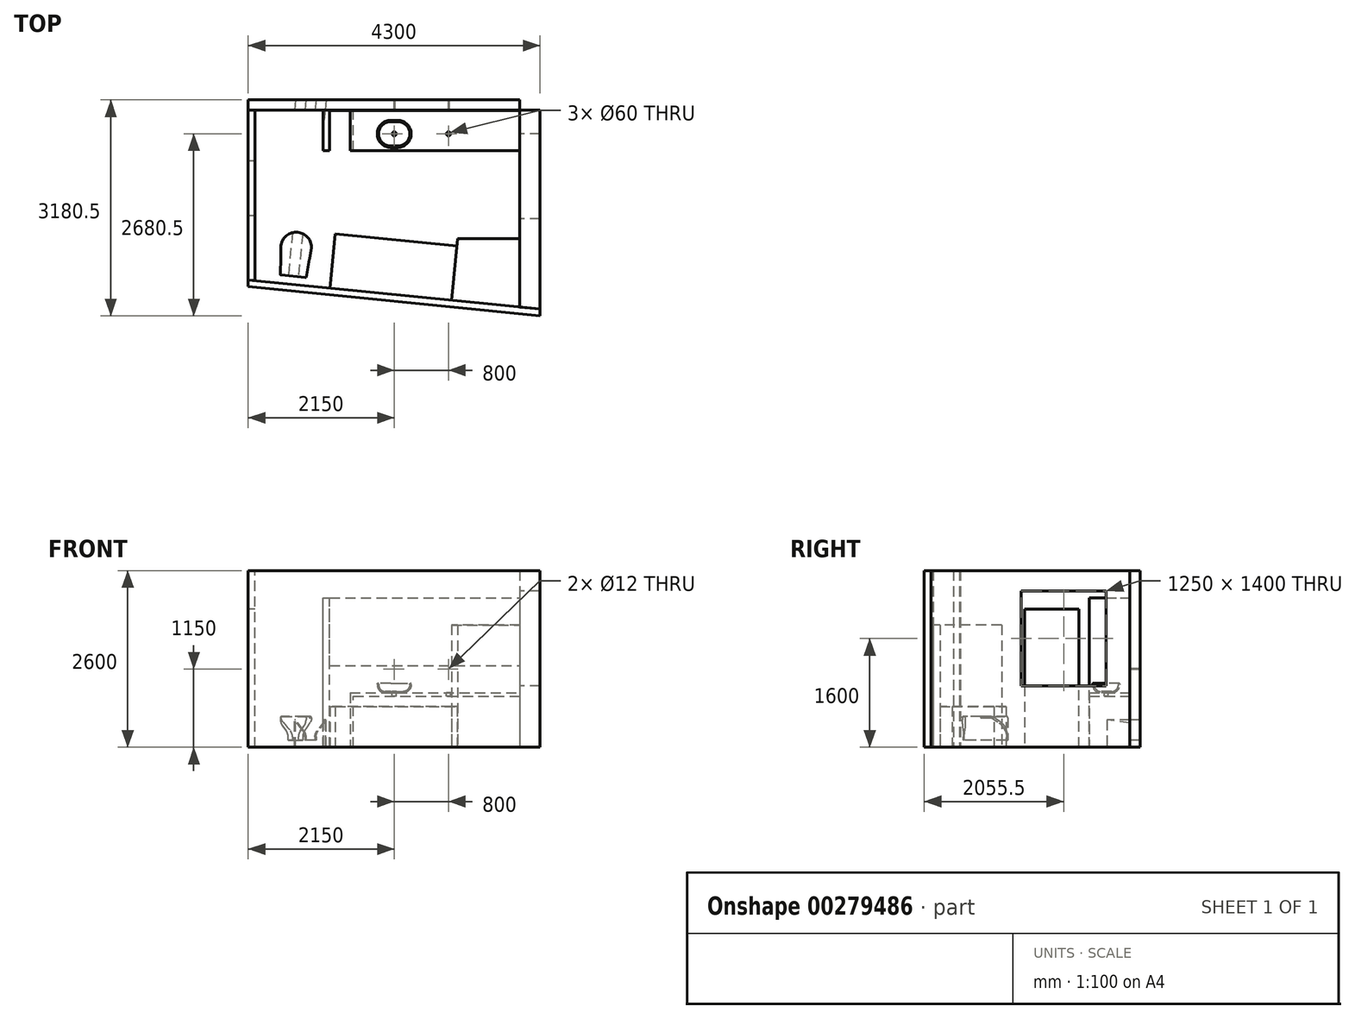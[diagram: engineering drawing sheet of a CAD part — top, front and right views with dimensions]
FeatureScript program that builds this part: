
annotation { "Feature Type Name" : "Feature", "Feature Type Description" : "" }
export const myFeature = defineFeature(function(context is Context, id is Id, definition is map)
    precondition{}
    {
        {
            var Q0;
            Q0=qCreatedBy(makeId("Front.planeOp"),FACE);
            var sketch = newSketch(context, id + "F0", { "sketchPlane" : qUnion([Q0])});
            skLineSegment(sketch, "E0.bottom", {"start": v(-1250, 800) * mm, "end": v(1250, 800) * mm});
            skLineSegment(sketch, "E0.top", {"start": v(-1250, 0) * mm, "end": v(1250, 0) * mm});
            skLineSegment(sketch, "E0.left", {"start": v(-1250, 800) * mm, "end": v(-1250, 0) * mm});
            skLineSegment(sketch, "E0.right", {"start": v(1250, 800) * mm, "end": v(1250, 0) * mm});
            skPoint(sketch, "E1", {"position": v(0, 800) * mm});
            skPoint(sketch, "E2", {"position": v(-1250, 400) * mm});
            skLineSegment(sketch, "E3", {"start": v(-1200, 0) * mm, "end": v(-1200, 750) * mm});
            skLineSegment(sketch, "E4", {"start": v(-1200, 750) * mm, "end": v(1250, 750) * mm});
            skSolve(sketch);
        }
        {
            var Q0;
            {var subQ1=sQuery(id+"F0.wireOp",EDGE,"E0.bottom");Q0=makeQuery(id+"F0.imprint","IMPRINT",FACE,{"disambiguationData":[TD([[makeQuery(id+"F0.imprint","IMPRINT",EDGE,{"derivedFrom":subQ1}),-1.0]])]});}
            extrude(context, id + "F1", {"entities" : qUnion([Q0]), "depth" : 600 * mm});
        }
        {
            var Q0;
            Q0=makeQuery(id+"F1.opExtrude","SWEPT_FACE",FACE,{"disambiguationData":[OSD([sQuery(id+"F0.wireOp",EDGE,"E0.bottom")])]});
            var sketch = newSketch(context, id + "F2", { "sketchPlane" : qUnion([Q0])});
            skLineSegment(sketch, "E5.0", {"start": v(-1250, 0) * mm, "end": v(1250, 0) * mm});
            skLineSegment(sketch, "E6.0", {"start": v(-1250, -600) * mm, "end": v(-1250, 0) * mm});
            skLineSegment(sketch, "E7.0", {"start": v(-1250, -600) * mm, "end": v(1250, -600) * mm});
            skLineSegment(sketch, "E8.0", {"start": v(1250, -600) * mm, "end": v(1250, 0) * mm});
            skLineSegment(sketch, "E9", {"start": v(-600, 54.18) * mm, "end": v(-600, -682.46) * mm, "construction": true});
            skLineSegment(sketch, "E10", {"start": v(200, 52.3) * mm, "end": v(200, -699.42) * mm, "construction": true});
            skLineSegment(sketch, "E11.bottom", {"start": v(-850, -150) * mm, "end": v(-350, -150) * mm});
            skLineSegment(sketch, "E11.top", {"start": v(-850, -550) * mm, "end": v(-350, -550) * mm});
            skLineSegment(sketch, "E11.left", {"start": v(-850, -150) * mm, "end": v(-850, -550) * mm});
            skLineSegment(sketch, "E11.right", {"start": v(-350, -150) * mm, "end": v(-350, -550) * mm});
            skLineSegment(sketch, "E12", {"start": v(-850, -350) * mm, "end": v(200, -350) * mm, "construction": true});
            skSolve(sketch);
        }
        {
            var Q0;
            Q0=makeQuery(id+"F2.imprint","IMPRINT",FACE,{"disambiguationData":[TD([[makeQuery(id+"F2.imprint","IMPRINT",EDGE,{"derivedFrom":sQuery(id+"F2.wireOp",EDGE,"E11.bottom")}),-1.0]])]});
            extrude(context, id + "F3", {"entities" : qUnion([Q0]), "depth" : 140 * mm});
        }
        {
            var Q0;
            Q0=makeQuery(id+"F3.opExtrude","SWEPT_EDGE",EDGE,{"disambiguationData":[OSD([sQuery(id+"F2.wireOp",EDGE,"E11.top"),sQuery(id+"F2.wireOp",EDGE,"E11.left")])]});
            var Q1;
            Q1=makeQuery(id+"F3.opExtrude","SWEPT_EDGE",EDGE,{"disambiguationData":[OSD([sQuery(id+"F2.wireOp",EDGE,"E11.top"),sQuery(id+"F2.wireOp",EDGE,"E11.right")])]});
            var Q2;
            Q2=makeQuery(id+"F3.opExtrude","SWEPT_EDGE",EDGE,{"disambiguationData":[OSD([sQuery(id+"F2.wireOp",EDGE,"E11.bottom"),sQuery(id+"F2.wireOp",EDGE,"E11.right")])]});
            var Q3;
            Q3=makeQuery(id+"F3.opExtrude","SWEPT_EDGE",EDGE,{"disambiguationData":[OSD([sQuery(id+"F2.wireOp",EDGE,"E11.bottom"),sQuery(id+"F2.wireOp",EDGE,"E11.left")])]});
            fillet(context, id + "F4", {"entities" : qUnion([Q0, Q1, Q2, Q3]), "radius" : 200 * mm, "tangentPropagation" : true, "allowEdgeOverflow" : false});
        }
        {
            var Q0;
            {var subQ0=sQuery(id+"F2.wireOp",EDGE,"E11.right");var subQ1=sQuery(id+"F2.wireOp",EDGE,"E11.bottom");Q0=makeQuery(id+"F4.opFillet","BLEND_EDGE",EDGE,{"blendedFrom":[makeQuery(id+"F3.opExtrude","SWEPT_EDGE",EDGE,{"disambiguationData":[OSD([subQ1,subQ0])]}),makeQuery(id+"F3.opExtrude","CAP_FACE",FACE,{"disambiguationData":[OSD([subQ1,sQuery(id+"F2.wireOp",EDGE,"E11.top"),sQuery(id+"F2.wireOp",EDGE,"E11.left"),subQ0])],"isStart":true})],"blendedInto":[makeQuery(id+"F3.opExtrude","CAP_FACE",FACE,{"disambiguationData":[OSD([subQ1,sQuery(id+"F2.wireOp",EDGE,"E11.top"),sQuery(id+"F2.wireOp",EDGE,"E11.left"),subQ0])],"isStart":true})]});}
            var Q1;
            Q1=makeQuery(id+"F3.opExtrude","CAP_EDGE",EDGE,{"disambiguationData":[OSD([sQuery(id+"F2.wireOp",EDGE,"E11.top")])],"isStart":true});
            var Q2;
            {var subQ0=sQuery(id+"F2.wireOp",EDGE,"E11.left");var subQ1=sQuery(id+"F2.wireOp",EDGE,"E11.bottom");Q2=makeQuery(id+"F4.opFillet","BLEND_EDGE",EDGE,{"blendedFrom":[makeQuery(id+"F3.opExtrude","SWEPT_EDGE",EDGE,{"disambiguationData":[OSD([subQ1,subQ0])]}),makeQuery(id+"F3.opExtrude","CAP_FACE",FACE,{"disambiguationData":[OSD([subQ1,sQuery(id+"F2.wireOp",EDGE,"E11.top"),subQ0,sQuery(id+"F2.wireOp",EDGE,"E11.right")])],"isStart":true})],"blendedInto":[makeQuery(id+"F3.opExtrude","CAP_FACE",FACE,{"disambiguationData":[OSD([subQ1,sQuery(id+"F2.wireOp",EDGE,"E11.top"),subQ0,sQuery(id+"F2.wireOp",EDGE,"E11.right")])],"isStart":true})]});}
            var Q3;
            Q3=makeQuery(id+"F3.opExtrude","CAP_EDGE",EDGE,{"disambiguationData":[OSD([sQuery(id+"F2.wireOp",EDGE,"E11.bottom")])],"isStart":true});
            fillet(context, id + "F5", {"entities" : qUnion([Q0, Q1, Q2, Q3]), "radius" : 120 * mm, "tangentPropagation" : true, "allowEdgeOverflow" : false});
        }
        {
            var Q0;
            Q0=makeQuery(id+"F3.opExtrude","CAP_FACE",FACE,{"disambiguationData":[OSD([sQuery(id+"F2.wireOp",EDGE,"E11.bottom"),sQuery(id+"F2.wireOp",EDGE,"E11.top"),sQuery(id+"F2.wireOp",EDGE,"E11.left"),sQuery(id+"F2.wireOp",EDGE,"E11.right")])],"isStart":false});
            shell(context, id + "F6", {"entities" : qUnion([Q0]), "thickness" : 20 * mm});
        }
        {
            var Q0;
            {var subQ0=sQuery(id+"F2.wireOp",EDGE,"E11.right");var subQ1=sQuery(id+"F2.wireOp",EDGE,"E11.bottom");Q0=makeQuery(id+"F4.opFillet","BLEND_EDGE",EDGE,{"blendedFrom":[makeQuery(id+"F3.opExtrude","SWEPT_EDGE",EDGE,{"disambiguationData":[OSD([subQ1,subQ0])]}),makeQuery(id+"F3.opExtrude","CAP_FACE",FACE,{"disambiguationData":[OSD([subQ1,sQuery(id+"F2.wireOp",EDGE,"E11.top"),sQuery(id+"F2.wireOp",EDGE,"E11.left"),subQ0])],"isStart":false})],"blendedInto":[makeQuery(id+"F3.opExtrude","CAP_FACE",FACE,{"disambiguationData":[OSD([subQ1,sQuery(id+"F2.wireOp",EDGE,"E11.top"),sQuery(id+"F2.wireOp",EDGE,"E11.left"),subQ0])],"isStart":false})]});}
            var Q1;
            Q1=makeQuery(id+"F3.opExtrude","CAP_EDGE",EDGE,{"disambiguationData":[OSD([sQuery(id+"F2.wireOp",EDGE,"E11.bottom")])],"isStart":false});
            var Q2;
            {var subQ0=sQuery(id+"F2.wireOp",EDGE,"E11.left");var subQ1=sQuery(id+"F2.wireOp",EDGE,"E11.bottom");Q2=makeQuery(id+"F4.opFillet","BLEND_EDGE",EDGE,{"blendedFrom":[makeQuery(id+"F3.opExtrude","SWEPT_EDGE",EDGE,{"disambiguationData":[OSD([subQ1,subQ0])]}),makeQuery(id+"F3.opExtrude","CAP_FACE",FACE,{"disambiguationData":[OSD([subQ1,sQuery(id+"F2.wireOp",EDGE,"E11.top"),subQ0,sQuery(id+"F2.wireOp",EDGE,"E11.right")])],"isStart":false})],"blendedInto":[makeQuery(id+"F3.opExtrude","CAP_FACE",FACE,{"disambiguationData":[OSD([subQ1,sQuery(id+"F2.wireOp",EDGE,"E11.top"),subQ0,sQuery(id+"F2.wireOp",EDGE,"E11.right")])],"isStart":false})]});}
            var Q3;
            Q3=makeQuery(id+"F3.opExtrude","CAP_EDGE",EDGE,{"disambiguationData":[OSD([sQuery(id+"F2.wireOp",EDGE,"E11.top")])],"isStart":false});
            fillet(context, id + "F7", {"entities" : qUnion([Q0, Q1, Q2, Q3]), "radius" : 10 * mm, "tangentPropagation" : true, "allowEdgeOverflow" : false});
        }
        {
            var Q0;
            {var subQ0=sQuery(id+"F2.wireOp",EDGE,"E11.top");Q0=makeQuery(id+"F6.opShell","OFFSET_EDGE",EDGE,{"disambiguationData":[OSD([subQ0]),TDD([makeQuery(id+"F3.opExtrude","CAP_EDGE",EDGE,{"disambiguationData":[OSD([subQ0])],"isStart":false})])]});}
            var Q1;
            {var subQ0=sQuery(id+"F2.wireOp",EDGE,"E11.right");var subQ1=sQuery(id+"F2.wireOp",EDGE,"E11.left");var subQ2=sQuery(id+"F2.wireOp",EDGE,"E11.top");var subQ3=sQuery(id+"F2.wireOp",EDGE,"E11.bottom");Q1=makeQuery(id+"F6.opShell","OFFSET_EDGE",EDGE,{"disambiguationData":[OSD([subQ3,subQ2,subQ1,subQ0]),TDD([makeQuery(id+"F4.opFillet","BLEND_EDGE",EDGE,{"blendedFrom":[makeQuery(id+"F3.opExtrude","SWEPT_EDGE",EDGE,{"disambiguationData":[OSD([subQ3,subQ1])]}),makeQuery(id+"F3.opExtrude","CAP_FACE",FACE,{"disambiguationData":[OSD([subQ3,subQ2,subQ1,subQ0])],"isStart":false})],"blendedInto":[makeQuery(id+"F3.opExtrude","CAP_FACE",FACE,{"disambiguationData":[OSD([subQ3,subQ2,subQ1,subQ0])],"isStart":false})]})])]});}
            var Q2;
            {var subQ0=sQuery(id+"F2.wireOp",EDGE,"E11.right");var subQ1=sQuery(id+"F2.wireOp",EDGE,"E11.left");var subQ2=sQuery(id+"F2.wireOp",EDGE,"E11.top");var subQ3=sQuery(id+"F2.wireOp",EDGE,"E11.bottom");Q2=makeQuery(id+"F6.opShell","OFFSET_EDGE",EDGE,{"disambiguationData":[OSD([subQ3,subQ2,subQ1,subQ0]),TDD([makeQuery(id+"F4.opFillet","BLEND_EDGE",EDGE,{"blendedFrom":[makeQuery(id+"F3.opExtrude","SWEPT_EDGE",EDGE,{"disambiguationData":[OSD([subQ3,subQ0])]}),makeQuery(id+"F3.opExtrude","CAP_FACE",FACE,{"disambiguationData":[OSD([subQ3,subQ2,subQ1,subQ0])],"isStart":false})],"blendedInto":[makeQuery(id+"F3.opExtrude","CAP_FACE",FACE,{"disambiguationData":[OSD([subQ3,subQ2,subQ1,subQ0])],"isStart":false})]})])]});}
            var Q3;
            {var subQ0=sQuery(id+"F2.wireOp",EDGE,"E11.bottom");Q3=makeQuery(id+"F6.opShell","OFFSET_EDGE",EDGE,{"disambiguationData":[OSD([subQ0]),TDD([makeQuery(id+"F3.opExtrude","CAP_EDGE",EDGE,{"disambiguationData":[OSD([subQ0])],"isStart":false})])]});}
            fillet(context, id + "F8", {"entities" : qUnion([Q0, Q1, Q2, Q3]), "radius" : 10 * mm, "tangentPropagation" : true, "allowEdgeOverflow" : false});
        }
        {
            var Q0;
            {var subQ0=sQuery(id+"F2.wireOp",EDGE,"E11.right");var subQ1=sQuery(id+"F2.wireOp",EDGE,"E11.left");var subQ2=sQuery(id+"F2.wireOp",EDGE,"E11.top");var subQ3=sQuery(id+"F2.wireOp",EDGE,"E11.bottom");Q0=makeQuery(id+"F6.opShell","OFFSET_FACE",FACE,{"disambiguationData":[OSD([subQ3,subQ2,subQ1,subQ0]),TDD([makeQuery(id+"F3.opExtrude","CAP_FACE",FACE,{"disambiguationData":[OSD([subQ3,subQ2,subQ1,subQ0])],"isStart":true})])]});}
            var sketch = newSketch(context, id + "F9", { "sketchPlane" : qUnion([Q0])});
            skLineSegment(sketch, "E13.0", {"start": v(-650, -270) * mm, "end": v(-550, -270) * mm});
            skLineSegment(sketch, "E14.0", {"start": v(-550, -430) * mm, "end": v(-650, -430) * mm});
            skLineSegment(sketch, "E15", {"start": v(-600, -430) * mm, "end": v(-600, -270) * mm, "construction": true});
            skPoint(sketch, "E16", {"position": v(-600, -350) * mm});
            skCircle(sketch, "E17", {"center": v(-600, -350) * mm, "radius": 30 * mm});
            skSolve(sketch);
        }
        {
            var Q0;
            Q0=makeQuery(id+"F9.imprint","IMPRINT",FACE,{"disambiguationData":[TD([[makeQuery(id+"F9.imprint","IMPRINT",EDGE,{"derivedFrom":sQuery(id+"F9.wireOp",EDGE,"E17")}),1.0]])]});
            extrude(context, id + "F10", {"entities" : qUnion([Q0]), "operationType" : NewBodyOperationType.REMOVE, "endBound" : BoundingType.THROUGH_ALL, "oppositeDirection" : true, "depth" : 25 * mm});
        }
        {
            var Q0;
            Q0=sQuery(id+"F2.wireOp",VERTEX,"E12.end");
            var Q1;
            Q1=makeQuery(id+"F1.opExtrude","SWEPT_BODY",BODY,{"disambiguationData":[OSD([sQuery(id+"F0.wireOp",EDGE,"E0.bottom"),sQuery(id+"F0.wireOp",EDGE,"E0.top"),sQuery(id+"F0.wireOp",EDGE,"E0.left"),sQuery(id+"F0.wireOp",EDGE,"E0.right"),sQuery(id+"F0.wireOp",EDGE,"E3"),sQuery(id+"F0.wireOp",EDGE,"E4")])]});
            hole(context, id + "F11", {"style" : HoleStyle.SIMPLE, "endStyle" : HoleEndStyle.BLIND, "holeDiameter" : 60 * mm, "holeDepth" : 170 * mm, "tappedDepth" : 12 * mm, "tapClearance" : 3, "locations" : qUnion([Q0]), "scope" : qUnion([Q1])});
        }
        {
            var Q0;
            Q0=makeQuery(id+"F1.opExtrude","CAP_FACE",FACE,{"disambiguationData":[OSD([sQuery(id+"F0.wireOp",EDGE,"E0.bottom"),sQuery(id+"F0.wireOp",EDGE,"E0.top"),sQuery(id+"F0.wireOp",EDGE,"E0.left"),sQuery(id+"F0.wireOp",EDGE,"E0.right"),sQuery(id+"F0.wireOp",EDGE,"E3"),sQuery(id+"F0.wireOp",EDGE,"E4")])],"isStart":true});
            var sketch = newSketch(context, id + "F12", { "sketchPlane" : qUnion([Q0])});
            skLineSegment(sketch, "E18.0", {"start": v(2750, 0) * mm, "end": v(-1250, 0) * mm});
            skLineSegment(sketch, "E19.0", {"start": v(-1250, 2600) * mm, "end": v(-1250, 0) * mm});
            skPoint(sketch, "E20.orphan", {"position": v(1200, 0) * mm});
            skPoint(sketch, "E21.orphan", {"position": v(-1250, 750) * mm});
            skLineSegment(sketch, "E22", {"start": v(-1250, 2600) * mm, "end": v(2750, 2600) * mm});
            skLineSegment(sketch, "E23", {"start": v(2750, 2600) * mm, "end": v(2750, 0) * mm});
            skPoint(sketch, "E24.orphan", {"position": v(1250, 0) * mm});
            skPoint(sketch, "E25.orphan", {"position": v(-1250, 800) * mm});
            skSolve(sketch);
        }
        {
            var Q0;
            {var subQ1=sQuery(id+"F12.wireOp",EDGE,"E22");Q0=makeQuery(id+"F12.imprint","IMPRINT",FACE,{"disambiguationData":[TD([[makeQuery(id+"F12.imprint","IMPRINT",EDGE,{"derivedFrom":subQ1}),-1.0]])]});}
            var Q1;
            {var subQ1=makeQuery(id+"F1.opExtrude","CAP_EDGE",EDGE,{"disambiguationData":[OSD([sQuery(id+"F0.wireOp",EDGE,"E3")])],"isStart":true});Q1=makeQuery(id+"F12.imprint","IMPRINT",FACE,{"disambiguationData":[TD([[makeQuery(id+"F12.imprint","IMPRINT",EDGE,{"derivedFrom":subQ1}),1.0]])]});}
            var Q2;
            {var subQ1=makeQuery(id+"F1.opExtrude","CAP_EDGE",EDGE,{"disambiguationData":[OSD([sQuery(id+"F0.wireOp",EDGE,"E0.bottom")])],"isStart":true});Q2=makeQuery(id+"F12.imprint","IMPRINT",FACE,{"disambiguationData":[TD([[makeQuery(id+"F12.imprint","IMPRINT",EDGE,{"derivedFrom":subQ1}),1.0]])]});}
            extrude(context, id + "F13", {"entities" : qUnion([Q0, Q1, Q2]), "depth" : 150 * mm});
        }
        {
            var Q0;
            Q0=makeQuery(id+"F13.opExtrude","CAP_FACE",FACE,{"disambiguationData":[OSD([sQuery(id+"F12.wireOp",EDGE,"E18.0"),sQuery(id+"F12.wireOp",EDGE,"E19.0"),sQuery(id+"F12.wireOp",EDGE,"E22"),sQuery(id+"F12.wireOp",EDGE,"E23")])],"isStart":true});
            var sketch = newSketch(context, id + "F14", { "sketchPlane" : qUnion([Q0])});
            skLineSegment(sketch, "E26.0", {"start": v(-2750, 0) * mm, "end": v(1250, 0) * mm});
            skLineSegment(sketch, "E27", {"start": v(-600, 0) * mm, "end": v(-600, 1150) * mm, "construction": true});
            skLineSegment(sketch, "E28", {"start": v(200, 0) * mm, "end": v(200, 1150) * mm, "construction": true});
            skLineSegment(sketch, "E29.0", {"start": v(-630, 800) * mm, "end": v(-570, 800) * mm});
            skLineSegment(sketch, "E30.0", {"start": v(170, 800) * mm, "end": v(230, 800) * mm});
            skPoint(sketch, "E31", {"position": v(-600, 800) * mm});
            skPoint(sketch, "E32", {"position": v(200, 800) * mm});
            skPoint(sketch, "E33", {"position": v(-600, 1150) * mm});
            skPoint(sketch, "E34", {"position": v(200, 1150) * mm});
            skSolve(sketch);
        }
        {
            var Q0;
            Q0=sQuery(id+"F14.wireOp",VERTEX,"E33");
            var Q1;
            Q1=sQuery(id+"F14.wireOp",VERTEX,"E34");
            var Q2;
            Q2=makeQuery(id+"F13.opExtrude","SWEPT_BODY",BODY,{"disambiguationData":[OSD([sQuery(id+"F12.wireOp",EDGE,"E18.0"),sQuery(id+"F12.wireOp",EDGE,"E19.0"),sQuery(id+"F12.wireOp",EDGE,"E22"),sQuery(id+"F12.wireOp",EDGE,"E23")])]});
            hole(context, id + "F15", {"style" : HoleStyle.SIMPLE, "endStyle" : HoleEndStyle.BLIND, "holeDiameter" : 12 * mm, "holeDepth" : 200 * mm, "tappedDepth" : 12 * mm, "tapClearance" : 3, "locations" : qUnion([Q0, Q1]), "scope" : qUnion([Q2])});
        }
        {
            var Q0;
            Q0=makeQuery(id+"F13.opExtrude","CAP_FACE",FACE,{"disambiguationData":[OSD([sQuery(id+"F12.wireOp",EDGE,"E18.0"),sQuery(id+"F12.wireOp",EDGE,"E19.0"),sQuery(id+"F12.wireOp",EDGE,"E22"),sQuery(id+"F12.wireOp",EDGE,"E23")])],"isStart":true});
            var sketch = newSketch(context, id + "F16", { "sketchPlane" : qUnion([Q0])});
            skLineSegment(sketch, "E35.0", {"start": v(-1250, 800) * mm, "end": v(-1250, 0) * mm});
            skLineSegment(sketch, "E36.bottom", {"start": v(-1650, 0) * mm, "end": v(-1550, 0) * mm});
            skLineSegment(sketch, "E36.top", {"start": v(-1650, 2200) * mm, "end": v(-1550, 2200) * mm});
            skLineSegment(sketch, "E36.left", {"start": v(-1650, 0) * mm, "end": v(-1650, 2200) * mm});
            skLineSegment(sketch, "E36.right", {"start": v(-1550, 0) * mm, "end": v(-1550, 2200) * mm});
            skLineSegment(sketch, "E37.bottom", {"start": v(-1550, 2200) * mm, "end": v(1250, 2200) * mm});
            skLineSegment(sketch, "E37.top", {"start": v(-1550, 1200) * mm, "end": v(1250, 1200) * mm});
            skLineSegment(sketch, "E37.left", {"start": v(-1550, 2200) * mm, "end": v(-1550, 1200) * mm});
            skLineSegment(sketch, "E37.right", {"start": v(1250, 2200) * mm, "end": v(1250, 1200) * mm});
            skLineSegment(sketch, "E38.bottom", {"start": v(-2750, 0) * mm, "end": v(-2650, 0) * mm});
            skLineSegment(sketch, "E38.top", {"start": v(-2750, 2600) * mm, "end": v(-2650, 2600) * mm});
            skLineSegment(sketch, "E38.left", {"start": v(-2750, 0) * mm, "end": v(-2750, 2600) * mm});
            skLineSegment(sketch, "E38.right", {"start": v(-2650, 0) * mm, "end": v(-2650, 2600) * mm});
            skSolve(sketch);
        }
        {
            var Q0;
            Q0=makeQuery(id+"F16.imprint","IMPRINT",FACE,{"disambiguationData":[TD([[makeQuery(id+"F16.imprint","IMPRINT",EDGE,{"derivedFrom":sQuery(id+"F16.wireOp",EDGE,"E37.bottom")}),-1.0]])]});
            extrude(context, id + "F17", {"entities" : qUnion([Q0]), "depth" : 8 * mm});
        }
        {
            var Q0;
            Q0=makeQuery(id+"F16.imprint","IMPRINT",FACE,{"disambiguationData":[TD([[makeQuery(id+"F16.imprint","IMPRINT",EDGE,{"derivedFrom":sQuery(id+"F16.wireOp",EDGE,"E36.bottom")}),1.0]])]});
            extrude(context, id + "F18", {"entities" : qUnion([Q0]), "depth" : 600 * mm});
        }
        {
            var Q0;
            Q0=makeQuery(id+"F16.imprint","IMPRINT",FACE,{"disambiguationData":[TD([[makeQuery(id+"F16.imprint","IMPRINT",EDGE,{"derivedFrom":sQuery(id+"F16.wireOp",EDGE,"E38.bottom")}),1.0]])]});
            extrude(context, id + "F19", {"entities" : qUnion([Q0]), "depth" : 750 * mm});
        }
        {
            var Q0;
            Q0=makeQuery(id+"F13.opExtrude","SWEPT_FACE",FACE,{"disambiguationData":[OSD([sQuery(id+"F12.wireOp",EDGE,"E18.0")])]});
            var sketch = newSketch(context, id + "F20", { "sketchPlane" : qUnion([Q0])});
            skLineSegment(sketch, "E39.0", {"start": v(-2750, 0) * mm, "end": v(1550, 0) * mm});
            skLineSegment(sketch, "E40.0", {"start": v(-2650, 750) * mm, "end": v(-2650, 0) * mm});
            skLineSegment(sketch, "E41.0", {"start": v(-2750, 750) * mm, "end": v(-2750, 0) * mm});
            skLineSegment(sketch, "E42", {"start": v(-2750, 2500) * mm, "end": v(1550, 2930) * mm});
            skLineSegment(sketch, "E43", {"start": v(1250, 0) * mm, "end": v(1250, 2900) * mm});
            skLineSegment(sketch, "E44", {"start": v(-2650, 1550) * mm, "end": v(-2650, 2510) * mm});
            skLineSegment(sketch, "E45", {"start": v(-2750, 1550) * mm, "end": v(-2750, 2600.5) * mm});
            skLineSegment(sketch, "E46", {"start": v(-2750, 1550) * mm, "end": v(-2650, 1550) * mm});
            skLineSegment(sketch, "E47", {"start": v(-2750, 2600.5) * mm, "end": v(1550, 3030.5) * mm});
            skLineSegment(sketch, "E48", {"start": v(1550, 0) * mm, "end": v(1550, 3030.5) * mm});
            skSolve(sketch);
        }
        {
            var Q0;
            {var subQ3=sQuery(id+"F20.wireOp",EDGE,"E44");Q0=makeQuery(id+"F20.imprint","IMPRINT",FACE,{"disambiguationData":[TD([[makeQuery(id+"F20.imprint","IMPRINT",EDGE,{"derivedFrom":subQ3}),1.0]])]});}
            extrude(context, id + "F21", {"entities" : qUnion([Q0]), "oppositeDirection" : true, "depth" : 2600 * mm});
        }
        {
            var Q0;
            {var subQ6=sQuery(id+"F20.wireOp",EDGE,"E47");Q0=makeQuery(id+"F20.imprint","IMPRINT",FACE,{"disambiguationData":[TD([[makeQuery(id+"F20.imprint","IMPRINT",EDGE,{"derivedFrom":subQ6}),-1.0]])]});}
            extrude(context, id + "F22", {"entities" : qUnion([Q0]), "oppositeDirection" : true, "depth" : 2600 * mm});
        }
        {
            var Q0;
            {var subQ0=sQuery(id+"F20.wireOp",EDGE,"E43");Q0=makeQuery(id+"F20.imprint","IMPRINT",FACE,{"disambiguationData":[TD([[makeQuery(id+"F20.imprint","IMPRINT",EDGE,{"derivedFrom":subQ0}),-1.0]])]});}
            extrude(context, id + "F23", {"entities" : qUnion([Q0]), "oppositeDirection" : true, "depth" : 2600 * mm});
        }
        {
            var Q0;
            Q0=makeQuery(id+"F23.opExtrude","SWEPT_FACE",FACE,{"disambiguationData":[OSD([sQuery(id+"F20.wireOp",EDGE,"E43")])]});
            var sketch = newSketch(context, id + "F24", { "sketchPlane" : qUnion([Q0])});
            skLineSegment(sketch, "E49.0", {"start": v(0, 2600) * mm, "end": v(0, 0) * mm});
            skLineSegment(sketch, "E50.0", {"start": v(0, 0) * mm, "end": v(2900, 0) * mm});
            skLineSegment(sketch, "E51.bottom", {"start": v(350, 2300) * mm, "end": v(1600, 2300) * mm});
            skLineSegment(sketch, "E51.top", {"start": v(350, 900) * mm, "end": v(1600, 900) * mm});
            skLineSegment(sketch, "E51.left", {"start": v(350, 2300) * mm, "end": v(350, 900) * mm});
            skLineSegment(sketch, "E51.right", {"start": v(1600, 2300) * mm, "end": v(1600, 900) * mm});
            skSolve(sketch);
        }
        {
            var Q0;
            Q0=makeQuery(id+"F24.imprint","IMPRINT",FACE,{"disambiguationData":[TD([[makeQuery(id+"F24.imprint","IMPRINT",EDGE,{"derivedFrom":sQuery(id+"F24.wireOp",EDGE,"E51.bottom")}),-1.0]])]});
            extrude(context, id + "F25", {"entities" : qUnion([Q0]), "operationType" : NewBodyOperationType.REMOVE, "endBound" : BoundingType.THROUGH_ALL, "oppositeDirection" : true, "depth" : 25 * mm});
        }
        {
            var Q0;
            Q0=makeQuery(id+"F19.opExtrude","CAP_FACE",FACE,{"disambiguationData":[OSD([sQuery(id+"F16.wireOp",EDGE,"E38.bottom"),sQuery(id+"F16.wireOp",EDGE,"E38.top"),sQuery(id+"F16.wireOp",EDGE,"E38.left"),sQuery(id+"F16.wireOp",EDGE,"E38.right")])],"isStart":false});
            var sketch = newSketch(context, id + "F26", { "sketchPlane" : qUnion([Q0])});
            skLineSegment(sketch, "E52.0", {"start": v(-2650, 0) * mm, "end": v(-2650, 2600) * mm});
            skLineSegment(sketch, "E53.0", {"start": v(-2750, 2600) * mm, "end": v(-2750, 0) * mm});
            skLineSegment(sketch, "E54.0", {"start": v(-2750, 0) * mm, "end": v(-2650, 0) * mm});
            skLineSegment(sketch, "E55.0", {"start": v(-2650, 2600) * mm, "end": v(-2750, 2600) * mm});
            skLineSegment(sketch, "E56", {"start": v(-2650, 2030) * mm, "end": v(-2750, 2030) * mm});
            skSolve(sketch);
        }
        {
            var Q0;
            {var subQ0=sQuery(id+"F26.wireOp",EDGE,"E55.0");Q0=makeQuery(id+"F26.imprint","IMPRINT",FACE,{"disambiguationData":[TD([[makeQuery(id+"F26.imprint","IMPRINT",EDGE,{"derivedFrom":subQ0}),1.0]])]});}
            var Q1;
            Q1=makeQuery(id+"F21.opExtrude","SWEPT_FACE",FACE,{"disambiguationData":[OSD([sQuery(id+"F20.wireOp",EDGE,"E46")])]});
            extrude(context, id + "F27", {"entities" : qUnion([Q0]), "operationType" : NewBodyOperationType.ADD, "endBound" : BoundingType.UP_TO_SURFACE, "endBoundEntityFace" : qUnion([Q1]), "depth" : 25 * mm});
        }
        {
            var Q0;
            Q0=makeQuery(id+"F23.opExtrude","CAP_FACE",FACE,{"disambiguationData":[OSD([sQuery(id+"F20.wireOp",EDGE,"E39.0"),sQuery(id+"F20.wireOp",EDGE,"E42"),sQuery(id+"F20.wireOp",EDGE,"E43"),sQuery(id+"F20.wireOp",EDGE,"E48")])],"isStart":true});
            var sketch = newSketch(context, id + "F28", { "sketchPlane" : qUnion([Q0])});
            skLineSegment(sketch, "E57.0", {"start": v(1250, 0) * mm, "end": v(1250, 2900) * mm});
            skLineSegment(sketch, "E58.0", {"start": v(245.01, 2799.5) * mm, "end": v(1250, 2900) * mm});
            skLineSegment(sketch, "E59", {"start": v(1250, 1890) * mm, "end": v(335.96, 1890) * mm});
            skLineSegment(sketch, "E60", {"start": v(335.96, 1890) * mm, "end": v(245.01, 2799.5) * mm});
            skPoint(sketch, "E61.orphan", {"position": v(-2750, 2500) * mm});
            skPoint(sketch, "E62.orphan", {"position": v(1550, 2930) * mm});
            skLineSegment(sketch, "E63", {"start": v(245.01, 2799.5) * mm, "end": v(-1546.05, 2620.4) * mm});
            skLineSegment(sketch, "E64", {"start": v(-1546.05, 2620.4) * mm, "end": v(-1466.45, 1824.36) * mm});
            skLineSegment(sketch, "E65", {"start": v(-1466.45, 1824.36) * mm, "end": v(324.62, 2003.47) * mm});
            skLineSegment(sketch, "E66", {"start": v(-1546.05, 2620.4) * mm, "end": v(-2650, 2510) * mm});
            skLineSegment(sketch, "E67.0", {"start": v(-2650, 1550) * mm, "end": v(-2650, 2510) * mm});
            skPoint(sketch, "E68", {"position": v(-2098.03, 2565.2) * mm});
            skLineSegment(sketch, "E69", {"start": v(-2098.03, 2565.2) * mm, "end": v(-2021.4, 1799.02) * mm, "construction": true});
            skLineSegment(sketch, "E70", {"start": v(-1534.11, 2501) * mm, "end": v(-2650, 2389.4) * mm});
            skCircle(sketch, "E71", {"center": v(-2043.8, 2022.9) * mm, "radius": 225 * mm});
            skLineSegment(sketch, "E72", {"start": v(-1822.58, 2064) * mm, "end": v(-1897.03, 2464.7) * mm});
            skLineSegment(sketch, "E73", {"start": v(-2268.77, 2019.38) * mm, "end": v(-2275.14, 2426.89) * mm});
            skLineSegment(sketch, "E74", {"start": v(-1897.03, 2464.7) * mm, "end": v(-2275.14, 2426.89) * mm, "construction": true});
            skPoint(sketch, "E75", {"position": v(-2086.09, 2445.8) * mm});
            skSolve(sketch);
        }
        {
            var Q0;
            {var subQ3=sQuery(id+"F28.wireOp",EDGE,"E63");Q0=makeQuery(id+"F28.imprint","IMPRINT",FACE,{"disambiguationData":[TD([[makeQuery(id+"F28.imprint","IMPRINT",EDGE,{"derivedFrom":subQ3}),1.0]])]});}
            extrude(context, id + "F29", {"entities" : qUnion([Q0]), "oppositeDirection" : true, "depth" : 600 * mm});
        }
        {
            var Q0;
            {var subQ0=sQuery(id+"F28.wireOp",EDGE,"E71");var subQ1=makeQuery(id+"F28.imprint","INTERSECT",VERTEX,{"derivedFrom":[subQ0,sQuery(id+"F28.wireOp",EDGE,"E72")]});Q0=makeQuery(id+"F28.imprint","IMPRINT",FACE,{"disambiguationData":[TD([[makeQuery(id+"F28.imprint","IMPRINT",EDGE,{"disambiguationData":[TD([[subQ1,-1.0]])],"derivedFrom":subQ0}),1.0]])]});}
            var Q1;
            {var subQ0=sQuery(id+"F28.wireOp",EDGE,"E72");Q1=makeQuery(id+"F28.imprint","IMPRINT",FACE,{"disambiguationData":[TD([[makeQuery(id+"F28.imprint","IMPRINT",EDGE,{"derivedFrom":subQ0}),1.0]])]});}
            extrude(context, id + "F30", {"entities" : qUnion([Q0, Q1]), "oppositeDirection" : true, "depth" : 450 * mm});
        }
        {
            var Q0;
            {var subQ3=sQuery(id+"F28.wireOp",EDGE,"E58.0");Q0=makeQuery(id+"F28.imprint","IMPRINT",FACE,{"disambiguationData":[TD([[makeQuery(id+"F28.imprint","IMPRINT",EDGE,{"derivedFrom":subQ3}),-1.0]])]});}
            extrude(context, id + "F31", {"entities" : qUnion([Q0]), "oppositeDirection" : true, "depth" : 1800 * mm});
        }
        {
            var Q0;
            Q0=makeQuery(id+"F30.opExtrude","SWEPT_FACE",FACE,{"disambiguationData":[OSD([sQuery(id+"F28.wireOp",EDGE,"E70")])]});
            var sketch = newSketch(context, id + "F32", { "sketchPlane" : qUnion([Q0])});
            skLineSegment(sketch, "E76.0", {"start": v(-1642.37, 450) * mm, "end": v(-2022.37, 450) * mm});
            skLineSegment(sketch, "E77.0", {"start": v(-2056.57, 450) * mm, "end": v(-2056.57, 0) * mm});
            skLineSegment(sketch, "E78.0", {"start": v(-1608.16, 450) * mm, "end": v(-1608.16, 0) * mm});
            skLineSegment(sketch, "E79", {"start": v(-1907.37, 100) * mm, "end": v(-1757.37, 100) * mm});
            skLineSegment(sketch, "E80", {"start": v(-2056.57, 400) * mm, "end": v(-1608.16, 400) * mm, "construction": true});
            skPoint(sketch, "E81", {"position": v(-1832.37, 400) * mm});
            skLineSegment(sketch, "E82", {"start": v(-1832.37, 400) * mm, "end": v(-1832.37, 0) * mm, "construction": true});
            skPoint(sketch, "E83", {"position": v(-1832.37, 100) * mm});
            skLineSegment(sketch, "E84.top", {"start": v(-1907.37, 200) * mm, "end": v(-1757.37, 200) * mm});
            skLineSegment(sketch, "E84.left", {"start": v(-1907.37, 100) * mm, "end": v(-1907.37, 200) * mm});
            skLineSegment(sketch, "E84.right", {"start": v(-1757.37, 100) * mm, "end": v(-1757.37, 200) * mm});
            skPoint(sketch, "E85.newPointA", {"position": v(-1608.16, 0) * mm});
            skLineSegment(sketch, "E86.0", {"start": v(-1608.16, 0) * mm, "end": v(-2056.57, 0) * mm});
            skLineSegment(sketch, "E87", {"start": v(-2056.57, 400) * mm, "end": v(-1907.37, 200) * mm});
            skPoint(sketch, "E88.orphan", {"position": v(-2022.37, 0) * mm});
            skPoint(sketch, "E89.orphan", {"position": v(-1642.37, 0) * mm});
            skLineSegment(sketch, "E90", {"start": v(-1757.37, 200) * mm, "end": v(-1608.16, 400) * mm});
            skSolve(sketch);
        }
        {
            var Q0;
            Q0=makeQuery(id+"F32.imprint","IMPRINT",FACE,{"disambiguationData":[TD([[makeQuery(id+"F32.imprint","IMPRINT",EDGE,{"derivedFrom":sQuery(id+"F32.wireOp",EDGE,"E79")}),-1.0]])]});
            var Q1;
            {var subQ0=sQuery(id+"F32.wireOp",EDGE,"E86.0");var subQ1=sQuery(id+"F32.wireOp",EDGE,"E77.0");var subQ2=makeQuery(id+"F32.imprint","INTERSECT",VERTEX,{"derivedFrom":[subQ1,subQ0]});Q1=makeQuery(id+"F32.imprint","IMPRINT",FACE,{"disambiguationData":[TD([[makeQuery(id+"F32.imprint","IMPRINT",EDGE,{"disambiguationData":[TD([[subQ2,1.0]])],"derivedFrom":subQ1}),1.0]])]});}
            var Q2;
            {var subQ0=sQuery(id+"F32.wireOp",EDGE,"E86.0");var subQ1=sQuery(id+"F32.wireOp",EDGE,"E78.0");var subQ2=makeQuery(id+"F32.imprint","INTERSECT",VERTEX,{"derivedFrom":[subQ1,subQ0]});Q2=makeQuery(id+"F32.imprint","IMPRINT",FACE,{"disambiguationData":[TD([[makeQuery(id+"F32.imprint","IMPRINT",EDGE,{"disambiguationData":[TD([[subQ2,1.0]])],"derivedFrom":subQ1}),-1.0]])]});}
            extrude(context, id + "F33", {"entities" : qUnion([Q0, Q1, Q2]), "operationType" : NewBodyOperationType.REMOVE, "endBound" : BoundingType.THROUGH_ALL, "oppositeDirection" : true, "depth" : 25 * mm});
        }
        {
            var Q0;
            Q0=makeQuery(id+"F33.boolean.opBoolean","INTERSECT",EDGE,{"derivedFrom":[makeQuery(id+"F30.opExtrude","SWEPT_FACE",FACE,{"disambiguationData":[OSD([sQuery(id+"F28.wireOp",EDGE,"E72")])]}),makeQuery(id+"F33.opExtrude","SWEPT_FACE",FACE,{"disambiguationData":[OSD([sQuery(id+"F32.wireOp",EDGE,"E90")])]})]});
            var Q1;
            Q1=makeQuery(id+"F33.boolean.opBoolean","INTERSECT",EDGE,{"derivedFrom":[makeQuery(id+"F30.opExtrude","SWEPT_FACE",FACE,{"disambiguationData":[OSD([sQuery(id+"F28.wireOp",EDGE,"E73")])]}),makeQuery(id+"F33.opExtrude","SWEPT_FACE",FACE,{"disambiguationData":[OSD([sQuery(id+"F32.wireOp",EDGE,"E87")])]})]});
            var Q2;
            Q2=makeQuery(id+"F33.boolean.opBoolean","COPY",EDGE,{"derivedFrom":makeQuery(id+"F33.opExtrude","SWEPT_EDGE",EDGE,{"disambiguationData":[OSD([sQuery(id+"F32.wireOp",EDGE,"E84.top"),sQuery(id+"F32.wireOp",EDGE,"E84.right"),sQuery(id+"F32.wireOp",EDGE,"E90")])]})});
            var Q3;
            Q3=makeQuery(id+"F33.boolean.opBoolean","COPY",EDGE,{"derivedFrom":makeQuery(id+"F33.opExtrude","SWEPT_EDGE",EDGE,{"disambiguationData":[OSD([sQuery(id+"F32.wireOp",EDGE,"E84.top"),sQuery(id+"F32.wireOp",EDGE,"E84.left"),sQuery(id+"F32.wireOp",EDGE,"E87")])]})});
            fillet(context, id + "F34", {"entities" : qUnion([Q0, Q1, Q2, Q3]), "radius" : 150 * mm, "tangentPropagation" : true, "allowEdgeOverflow" : false});
        }
        {
            var Q0;
            Q0=makeQuery(id+"F30.opExtrude","CAP_EDGE",EDGE,{"disambiguationData":[OSD([sQuery(id+"F28.wireOp",EDGE,"E71")])],"isStart":false});
            var Q1;
            Q1=makeQuery(id+"F30.opExtrude","CAP_EDGE",EDGE,{"disambiguationData":[OSD([sQuery(id+"F28.wireOp",EDGE,"E73")])],"isStart":false});
            var Q2;
            Q2=makeQuery(id+"F30.opExtrude","CAP_EDGE",EDGE,{"disambiguationData":[OSD([sQuery(id+"F28.wireOp",EDGE,"E72")])],"isStart":false});
            fillet(context, id + "F35", {"entities" : qUnion([Q0, Q1, Q2]), "radius" : 15 * mm, "tangentPropagation" : true, "allowEdgeOverflow" : false});
        }
    });
